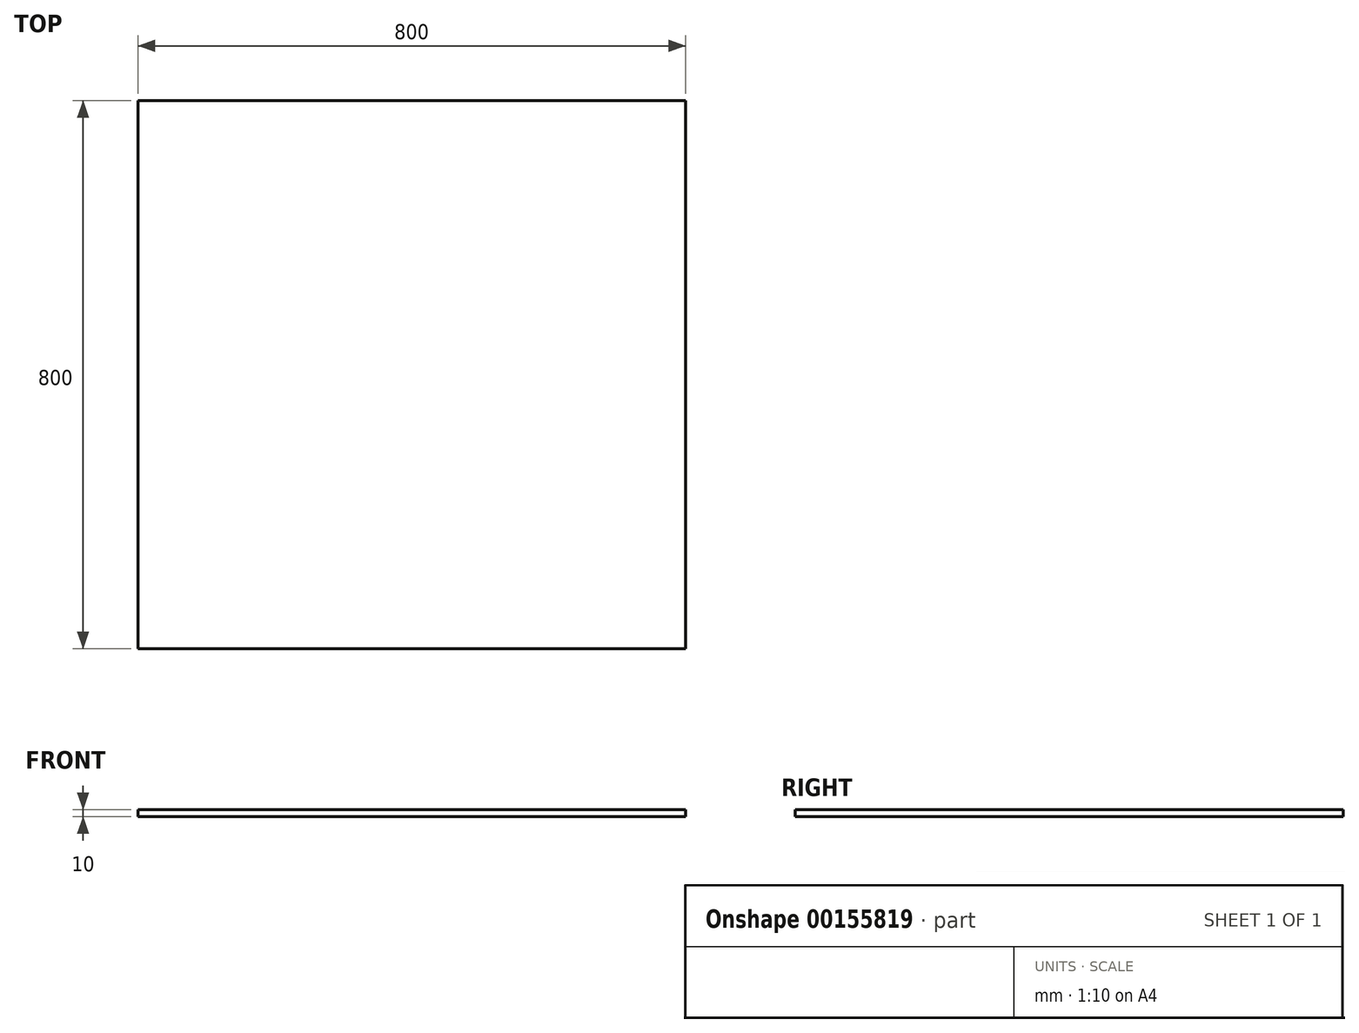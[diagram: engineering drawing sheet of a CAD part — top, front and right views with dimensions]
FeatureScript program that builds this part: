
annotation { "Feature Type Name" : "Feature", "Feature Type Description" : "" }
export const myFeature = defineFeature(function(context is Context, id is Id, definition is map)
    precondition{}
    {
        {
            var Q0;
            Q0=qCreatedBy(makeId("Top.planeOp"),FACE);
            var sketch = newSketch(context, id + "F0", { "sketchPlane" : qUnion([Q0])});
            skLineSegment(sketch, "E0.bottom", {"start": v(-400, -400) * mm, "end": v(400, -400) * mm});
            skLineSegment(sketch, "E0.top", {"start": v(-400, 400) * mm, "end": v(400, 400) * mm});
            skLineSegment(sketch, "E0.left", {"start": v(-400, -400) * mm, "end": v(-400, 400) * mm});
            skLineSegment(sketch, "E0.right", {"start": v(400, -400) * mm, "end": v(400, 400) * mm});
            skPoint(sketch, "E0.middle", {"position": v(0, 0) * mm});
            skSolve(sketch);
        }
        {
            var Q0;
            Q0 = qSketchRegion(id + "F0", true);
            extrude(context, id + "F1", {"entities" : qUnion([Q0]), "depth" : 10 * mm});
        }
    });
